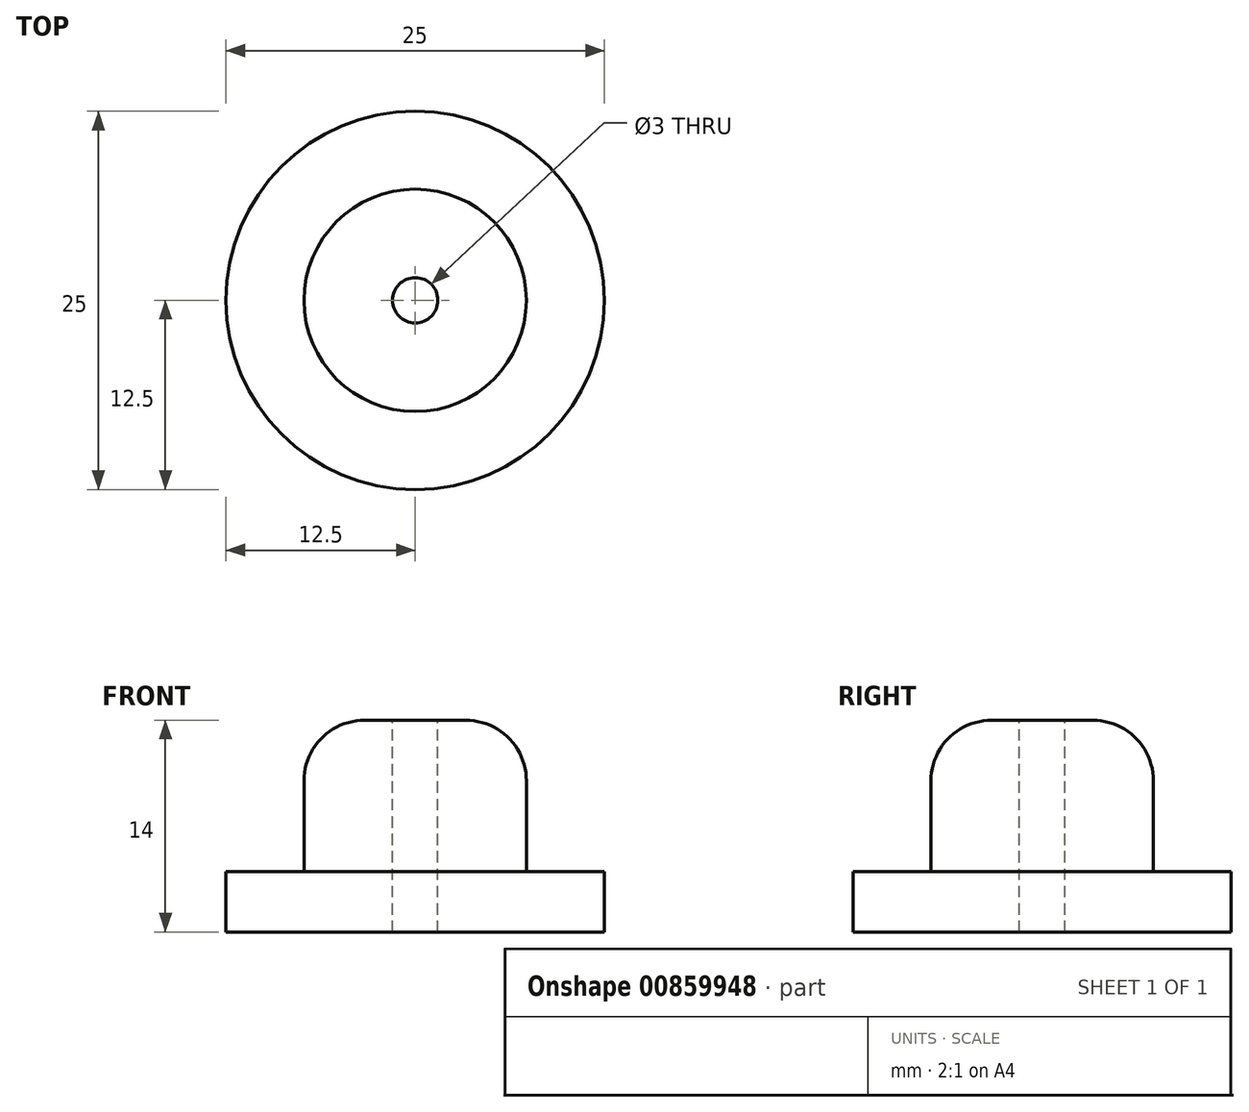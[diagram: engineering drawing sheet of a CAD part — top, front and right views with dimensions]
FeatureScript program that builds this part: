
annotation { "Feature Type Name" : "Feature", "Feature Type Description" : "" }
export const myFeature = defineFeature(function(context is Context, id is Id, definition is map)
    precondition{}
    {
        {
            var Q0;
            Q0=qCreatedBy(makeId("Top.planeOp"),FACE);
            var sketch = newSketch(context, id + "F0", { "sketchPlane" : qUnion([Q0])});
            skCircle(sketch, "E0", {"center": v(0, 0) * mm, "radius": 12.5 * mm});
            skSolve(sketch);
        }
        {
            var Q0;
            Q0=makeQuery(id+"F0.imprint","IMPRINT",FACE,{"disambiguationData":[TD([[makeQuery(id+"F0.imprint","IMPRINT",EDGE,{"derivedFrom":sQuery(id+"F0.wireOp",EDGE,"E0")}),1.0]])]});
            extrude(context, id + "F1", {"entities" : qUnion([Q0]), "depth" : 4 * mm, "offsetDistance" : 25 * mm});
        }
        {
            var Q0;
            Q0=makeQuery(id+"F1.opExtrude","CAP_FACE",FACE,{"disambiguationData":[OSD([sQuery(id+"F0.wireOp",EDGE,"E0")])],"isStart":false});
            var sketch = newSketch(context, id + "F2", { "sketchPlane" : qUnion([Q0])});
            skCircle(sketch, "E1", {"center": v(0, 0) * mm, "radius": 7.35 * mm});
            skSolve(sketch);
        }
        {
            var Q0;
            Q0=makeQuery(id+"F2.imprint","IMPRINT",FACE,{"disambiguationData":[TD([[makeQuery(id+"F2.imprint","IMPRINT",EDGE,{"derivedFrom":sQuery(id+"F2.wireOp",EDGE,"E1")}),1.0]])]});
            extrude(context, id + "F3", {"entities" : qUnion([Q0]), "operationType" : NewBodyOperationType.ADD, "depth" : 10 * mm, "offsetDistance" : 25 * mm});
        }
        {
            var Q0;
            Q0=makeQuery(id+"F3.opExtrude","CAP_FACE",FACE,{"disambiguationData":[OSD([sQuery(id+"F2.wireOp",EDGE,"E1")])],"isStart":false});
            var sketch = newSketch(context, id + "F4", { "sketchPlane" : qUnion([Q0])});
            skCircle(sketch, "E2", {"center": v(0, 0) * mm, "radius": 1.5 * mm});
            skSolve(sketch);
        }
        {
            var Q0;
            Q0=makeQuery(id+"F4.imprint","IMPRINT",FACE,{"disambiguationData":[TD([[makeQuery(id+"F4.imprint","IMPRINT",EDGE,{"derivedFrom":sQuery(id+"F4.wireOp",EDGE,"E2")}),1.0]])]});
            extrude(context, id + "F5", {"entities" : qUnion([Q0]), "operationType" : NewBodyOperationType.REMOVE, "endBound" : BoundingType.THROUGH_ALL, "oppositeDirection" : true, "depth" : 25 * mm, "offsetDistance" : 25 * mm});
        }
        {
            var Q0;
            Q0=makeQuery(id+"F3.opExtrude","CAP_EDGE",EDGE,{"disambiguationData":[OSD([sQuery(id+"F2.wireOp",EDGE,"E1")])],"isStart":false});
            fillet(context, id + "F6", {"entities" : qUnion([Q0]), "radius" : 4 * mm, "tangentPropagation" : true, "allowEdgeOverflow" : false});
        }
    });
